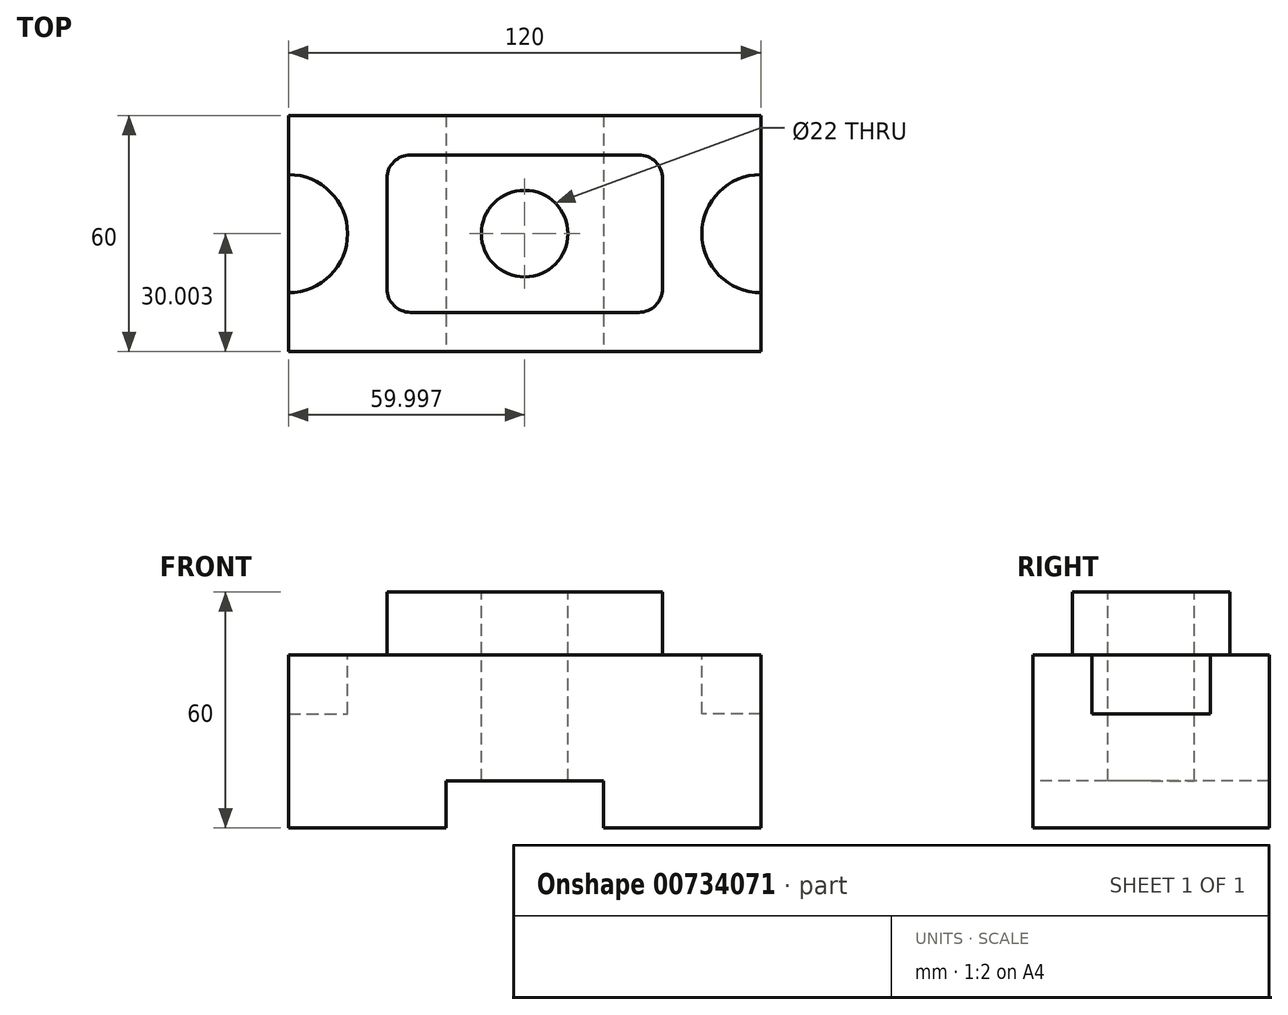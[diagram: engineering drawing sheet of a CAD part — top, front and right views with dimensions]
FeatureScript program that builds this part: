
annotation { "Feature Type Name" : "Feature", "Feature Type Description" : "" }
export const myFeature = defineFeature(function(context is Context, id is Id, definition is map)
    precondition{}
    {
        {
            var Q0;
            Q0=qCreatedBy(makeId("Top.planeOp"),FACE);
            var sketch = newSketch(context, id + "F0", { "sketchPlane" : qUnion([Q0])});
            skLineSegment(sketch, "E0.bottom", {"start": v(-86.46, 47.75) * mm, "end": v(33.54, 47.75) * mm});
            skLineSegment(sketch, "E0.top", {"start": v(-86.46, -12.25) * mm, "end": v(33.54, -12.25) * mm});
            skLineSegment(sketch, "E0.left", {"start": v(-86.46, 47.75) * mm, "end": v(-86.46, -12.25) * mm});
            skLineSegment(sketch, "E0.right", {"start": v(33.54, 47.75) * mm, "end": v(33.54, -12.25) * mm});
            skSolve(sketch);
        }
        {
            var Q0;
            Q0 = qSketchRegion(id + "F0", true);
            extrude(context, id + "F1", {"entities" : qUnion([Q0]), "depth" : 44 * mm, "offsetDistance" : 25 * mm});
        }
        {
            var Q0;
            Q0=makeQuery(id+"F1.opExtrude","CAP_FACE",FACE,{"disambiguationData":[OSD([sQuery(id+"F0.wireOp",EDGE,"E0.bottom"),sQuery(id+"F0.wireOp",EDGE,"E0.top"),sQuery(id+"F0.wireOp",EDGE,"E0.left"),sQuery(id+"F0.wireOp",EDGE,"E0.right")])],"isStart":false});
            var sketch = newSketch(context, id + "F2", { "sketchPlane" : qUnion([Q0])});
            skLineSegment(sketch, "E1", {"start": v(-55.46, -2.25) * mm, "end": v(2.54, -2.25) * mm});
            skLineSegment(sketch, "E2", {"start": v(8.54, 3.75) * mm, "end": v(8.54, 31.75) * mm});
            skLineSegment(sketch, "E3", {"start": v(2.54, 37.75) * mm, "end": v(-55.46, 37.75) * mm});
            skLineSegment(sketch, "E4", {"start": v(-61.46, 31.75) * mm, "end": v(-61.46, 3.75) * mm});
            skPoint(sketch, "E5.end.orphan", {"position": v(-61.46, -12.25) * mm});
            skPoint(sketch, "E6.visualSharp", {"position": v(-61.46, 37.75) * mm});
            skArc(sketch, "E6.filletArc", {"start": v(-55.46, 37.75) * mm, "mid": v(-59.7, 36) * mm, "end": v(-61.46, 31.75) * mm});
            skPoint(sketch, "E7.visualSharp", {"position": v(-61.46, -2.25) * mm});
            skArc(sketch, "E7.filletArc", {"start": v(-61.46, 3.75) * mm, "mid": v(-59.7, -0.5) * mm, "end": v(-55.46, -2.25) * mm});
            skPoint(sketch, "E8.visualSharp", {"position": v(8.54, -2.25) * mm});
            skArc(sketch, "E8.filletArc", {"start": v(2.54, -2.25) * mm, "mid": v(6.78, -0.5) * mm, "end": v(8.54, 3.75) * mm});
            skPoint(sketch, "E9.visualSharp", {"position": v(8.54, 37.75) * mm});
            skArc(sketch, "E9.filletArc", {"start": v(8.54, 31.75) * mm, "mid": v(6.78, 36) * mm, "end": v(2.54, 37.75) * mm});
            skSolve(sketch);
        }
        {
            var Q0;
            Q0 = qSketchRegion(id + "F2", true);
            extrude(context, id + "F3", {"entities" : qUnion([Q0]), "operationType" : NewBodyOperationType.ADD, "depth" : 16 * mm, "offsetDistance" : 25 * mm});
        }
        {
            var Q0;
            Q0=makeQuery(id+"F1.opExtrude","CAP_FACE",FACE,{"disambiguationData":[OSD([sQuery(id+"F0.wireOp",EDGE,"E0.bottom"),sQuery(id+"F0.wireOp",EDGE,"E0.top"),sQuery(id+"F0.wireOp",EDGE,"E0.left"),sQuery(id+"F0.wireOp",EDGE,"E0.right")])],"isStart":false});
            var sketch = newSketch(context, id + "F4", { "sketchPlane" : qUnion([Q0])});
            skLineSegment(sketch, "E10", {"start": v(33.54, -12.25) * mm, "end": v(33.54, 2.75) * mm});
            skArc(sketch, "E11", {"start": v(33.54, 32.75) * mm, "mid": v(18.54, 17.75) * mm, "end": v(33.54, 2.75) * mm});
            skArc(sketch, "E12", {"start": v(-86.46, 2.75) * mm, "mid": v(-71.46, 17.75) * mm, "end": v(-86.46, 32.75) * mm});
            skLineSegment(sketch, "E13.trimOffspring", {"start": v(33.54, 32.75) * mm, "end": v(33.54, 47.75) * mm});
            skLineSegment(sketch, "E14", {"start": v(-86.46, 47.75) * mm, "end": v(-86.46, 32.75) * mm});
            skLineSegment(sketch, "E15", {"start": v(-86.46, -12.25) * mm, "end": v(-86.46, 2.75) * mm});
            skLineSegment(sketch, "E16", {"start": v(33.54, 32.75) * mm, "end": v(33.54, 2.75) * mm});
            skLineSegment(sketch, "E17", {"start": v(-86.46, 32.75) * mm, "end": v(-86.46, 2.75) * mm});
            skSolve(sketch);
        }
        {
            var Q0;
            Q0 = qSketchRegion(id + "F4", true);
            extrude(context, id + "F5", {"entities" : qUnion([Q0]), "operationType" : NewBodyOperationType.REMOVE, "oppositeDirection" : true, "depth" : 15 * mm, "offsetDistance" : 25 * mm});
        }
        {
            var Q0;
            Q0=makeQuery(id+"F1.opExtrude","SWEPT_FACE",FACE,{"disambiguationData":[OSD([sQuery(id+"F0.wireOp",EDGE,"E0.top")])]});
            var sketch = newSketch(context, id + "F6", { "sketchPlane" : qUnion([Q0])});
            skLineSegment(sketch, "E18", {"start": v(-86.46, 0) * mm, "end": v(-46.46, 0) * mm});
            skLineSegment(sketch, "E19", {"start": v(-46.46, 0) * mm, "end": v(-46.46, 12) * mm});
            skLineSegment(sketch, "E20", {"start": v(-46.46, 12) * mm, "end": v(-6.46, 12) * mm});
            skLineSegment(sketch, "E21", {"start": v(-6.46, 12) * mm, "end": v(-6.46, 0) * mm});
            skLineSegment(sketch, "E22", {"start": v(-6.46, 0) * mm, "end": v(-46.46, 0) * mm});
            skSolve(sketch);
        }
        {
            var Q0;
            Q0 = qSketchRegion(id + "F6", true);
            extrude(context, id + "F7", {"entities" : qUnion([Q0]), "operationType" : NewBodyOperationType.REMOVE, "oppositeDirection" : true, "depth" : 60 * mm, "offsetDistance" : 25 * mm});
        }
        {
            var Q0;
            Q0=makeQuery(id+"F3.opExtrude","CAP_FACE",FACE,{"disambiguationData":[OSD([sQuery(id+"F2.wireOp",EDGE,"E1"),sQuery(id+"F2.wireOp",EDGE,"E2"),sQuery(id+"F2.wireOp",EDGE,"E3"),sQuery(id+"F2.wireOp",EDGE,"E4"),sQuery(id+"F2.wireOp",EDGE,"E6.filletArc"),sQuery(id+"F2.wireOp",EDGE,"E7.filletArc"),sQuery(id+"F2.wireOp",EDGE,"E8.filletArc"),sQuery(id+"F2.wireOp",EDGE,"E9.filletArc")])],"isStart":false});
            var sketch = newSketch(context, id + "F8", { "sketchPlane" : qUnion([Q0])});
            skLineSegment(sketch, "E23", {"start": v(-61.46, 17.75) * mm, "end": v(-61.46, 3.75) * mm});
            skCircle(sketch, "E24", {"center": v(-26.46, 17.75) * mm, "radius": 11 * mm});
            skPoint(sketch, "E25.start.orphan", {"position": v(8.54, 17.75) * mm});
            skSolve(sketch);
        }
        {
            var Q0;
            Q0 = qSketchRegion(id + "F8", true);
            extrude(context, id + "F9", {"entities" : qUnion([Q0]), "operationType" : NewBodyOperationType.REMOVE, "endBound" : BoundingType.THROUGH_ALL, "oppositeDirection" : true, "depth" : 38 * mm, "offsetDistance" : 25 * mm});
        }
    });
